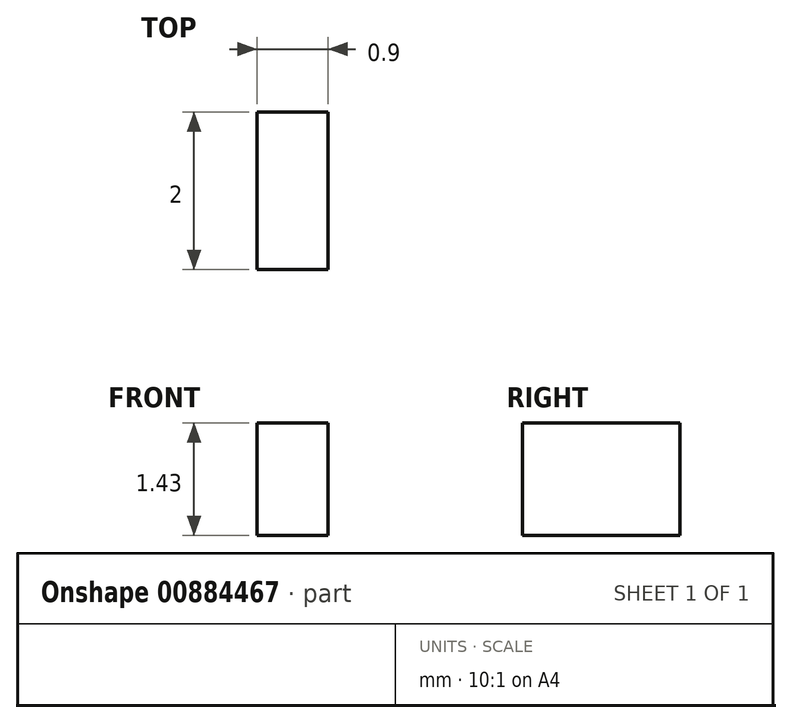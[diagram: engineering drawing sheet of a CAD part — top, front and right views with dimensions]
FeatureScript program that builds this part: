
annotation { "Feature Type Name" : "Feature", "Feature Type Description" : "" }
export const myFeature = defineFeature(function(context is Context, id is Id, definition is map)
    precondition{}
    {
        {
            var Q0;
            Q0=qCreatedBy(makeId("Front.planeOp"),FACE);
            var sketch = newSketch(context, id + "F0", { "sketchPlane" : qUnion([Q0])});
            skLineSegment(sketch, "E0", {"start": v(-19.5, 8.4) * mm, "end": v(0.44, 8.4) * mm});
            skLineSegment(sketch, "E1", {"start": v(0.55, 14.78) * mm, "end": v(-9.99, 14.78) * mm});
            skPoint(sketch, "E2.center.orphan", {"position": v(3.84, 8.53) * mm});
            skPoint(sketch, "E3.orphan", {"position": v(3.84, 12.67) * mm});
            skArc(sketch, "E4", {"start": v(0.44, 8.4) * mm, "mid": v(3.46, 11.82) * mm, "end": v(0, 14.78) * mm});
            skPoint(sketch, "E5.orphan", {"position": v(3.84, 14.78) * mm});
            skPoint(sketch, "E6.orphan", {"position": v(3.84, 8.4) * mm});
            skArc(sketch, "E7", {"start": v(-20.45, 14.78) * mm, "mid": v(-17.53, 12) * mm, "end": v(-13.66, 13.17) * mm});
            skPoint(sketch, "E8.visualSharp", {"position": v(-12.76, 14.78) * mm});
            skArc(sketch, "E8.filletArc", {"start": v(-9.99, 14.78) * mm, "mid": v(-12, 14.36) * mm, "end": v(-13.66, 13.17) * mm});
            skLineSegment(sketch, "E9.bottom", {"start": v(-19.5, 7.77) * mm, "end": v(-20.4, 7.77) * mm});
            skLineSegment(sketch, "E9.top", {"start": v(-19.5, 9.2) * mm, "end": v(-20.4, 9.2) * mm});
            skLineSegment(sketch, "E9.left", {"start": v(-19.5, 7.77) * mm, "end": v(-19.5, 9.2) * mm});
            skLineSegment(sketch, "E9.right", {"start": v(-20.4, 7.77) * mm, "end": v(-20.4, 9.2) * mm});
            skSolve(sketch);
        }
        {
            var Q0;
            Q0=makeQuery(id+"F0.imprint","IMPRINT",FACE,{"disambiguationData":[TD([[makeQuery(id+"F0.imprint","IMPRINT",EDGE,{"derivedFrom":sQuery(id+"F0.wireOp",EDGE,"OeCbsM0n-YI4P-pmDI-EALn-POEhlDsp5knm")}),1.0]])]});
            var Q1;
            {var subQ3=sQuery(id+"F0.wireOp",EDGE,"E9.bottom");Q1=makeQuery(id+"F0.imprint","IMPRINT",FACE,{"disambiguationData":[TD([[makeQuery(id+"F0.imprint","IMPRINT",EDGE,{"derivedFrom":subQ3}),-1.0]])]});}
            extrude(context, id + "F1", {"entities" : qUnion([Q0, Q1]), "depth" : 2 * mm, "offsetDistance" : 25 * mm});
        }
    });
